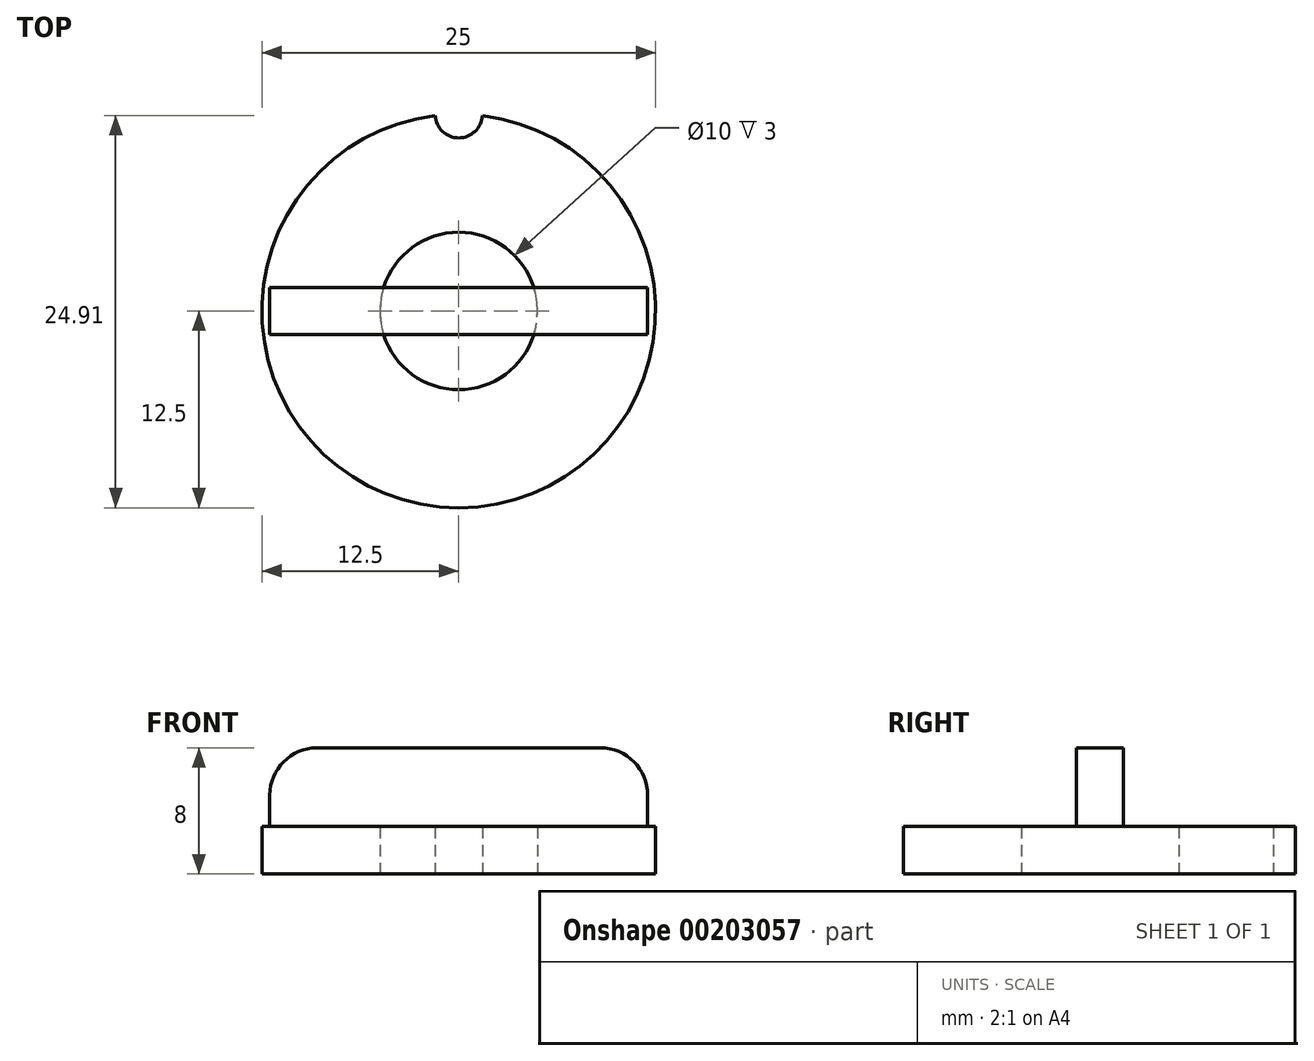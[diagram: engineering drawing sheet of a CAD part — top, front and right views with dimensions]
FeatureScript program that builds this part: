
annotation { "Feature Type Name" : "Feature", "Feature Type Description" : "" }
export const myFeature = defineFeature(function(context is Context, id is Id, definition is map)
    precondition{}
    {
        {
            var Q0;
            Q0=qCreatedBy(makeId("Top.planeOp"),FACE);
            var sketch = newSketch(context, id + "F0", { "sketchPlane" : qUnion([Q0])});
            skCircle(sketch, "E0", {"center": v(0, 0) * mm, "radius": 12.5 * mm});
            skCircle(sketch, "E1", {"center": v(0, 12.5) * mm, "radius": 1.5 * mm});
            skSolve(sketch);
        }
        {
            var Q0;
            {var subQ0=sQuery(id+"F0.wireOp",EDGE,"E1");var subQ1=sQuery(id+"F0.wireOp",EDGE,"E0");var subQ2=makeQuery(id+"F0.imprint","INTERSECT",VERTEX,{"disambiguationData":[OD(0.0)],"derivedFrom":[subQ1,subQ0]});Q0=makeQuery(id+"F0.imprint","IMPRINT",FACE,{"disambiguationData":[TD([[makeQuery(id+"F0.imprint","IMPRINT",EDGE,{"disambiguationData":[TD([[subQ2,-1.0]])],"derivedFrom":subQ1}),1.0]])]});}
            extrude(context, id + "F1", {"entities" : qUnion([Q0]), "depth" : 3 * mm});
        }
        {
            var Q0;
            Q0=makeQuery(id+"F1.opExtrude","CAP_FACE",FACE,{"disambiguationData":[OSD([sQuery(id+"F0.wireOp",EDGE,"E0"),sQuery(id+"F0.wireOp",EDGE,"E1")])],"isStart":false});
            var sketch = newSketch(context, id + "F2", { "sketchPlane" : qUnion([Q0])});
            skLineSegment(sketch, "E2.bottom", {"start": v(12, -1.5) * mm, "end": v(-12, -1.5) * mm});
            skLineSegment(sketch, "E2.top", {"start": v(12, 1.5) * mm, "end": v(-12, 1.5) * mm});
            skLineSegment(sketch, "E2.left", {"start": v(12, -1.5) * mm, "end": v(12, 1.5) * mm});
            skLineSegment(sketch, "E2.right", {"start": v(-12, -1.5) * mm, "end": v(-12, 1.5) * mm});
            skPoint(sketch, "E2.middle", {"position": v(0, 0) * mm});
            skSolve(sketch);
        }
        {
            var Q0;
            Q0 = qSketchRegion(id + "F2", true);
            extrude(context, id + "F3", {"entities" : qUnion([Q0]), "operationType" : NewBodyOperationType.ADD, "depth" : 5 * mm});
        }
        {
            var Q0;
            Q0=makeQuery(id+"F1.opExtrude","CAP_FACE",FACE,{"disambiguationData":[OSD([sQuery(id+"F0.wireOp",EDGE,"E0"),sQuery(id+"F0.wireOp",EDGE,"E1")])],"isStart":true});
            var sketch = newSketch(context, id + "F4", { "sketchPlane" : qUnion([Q0])});
            skCircle(sketch, "E3", {"center": v(0, 0) * mm, "radius": 5 * mm});
            skSolve(sketch);
        }
        {
            var Q0;
            Q0 = qSketchRegion(id + "F4", true);
            extrude(context, id + "F5", {"entities" : qUnion([Q0]), "operationType" : NewBodyOperationType.REMOVE, "oppositeDirection" : true, "depth" : 3 * mm});
        }
        {
            var Q0;
            Q0=makeQuery(id+"F3.opExtrude","CAP_EDGE",EDGE,{"disambiguationData":[OSD([sQuery(id+"F2.wireOp",EDGE,"E2.left")])],"isStart":false});
            var Q1;
            Q1=makeQuery(id+"F3.opExtrude","CAP_EDGE",EDGE,{"disambiguationData":[OSD([sQuery(id+"F2.wireOp",EDGE,"E2.right")])],"isStart":false});
            fillet(context, id + "F6", {"entities" : qUnion([Q0, Q1]), "radius" : 3 * mm, "tangentPropagation" : true, "allowEdgeOverflow" : false});
        }
    });
